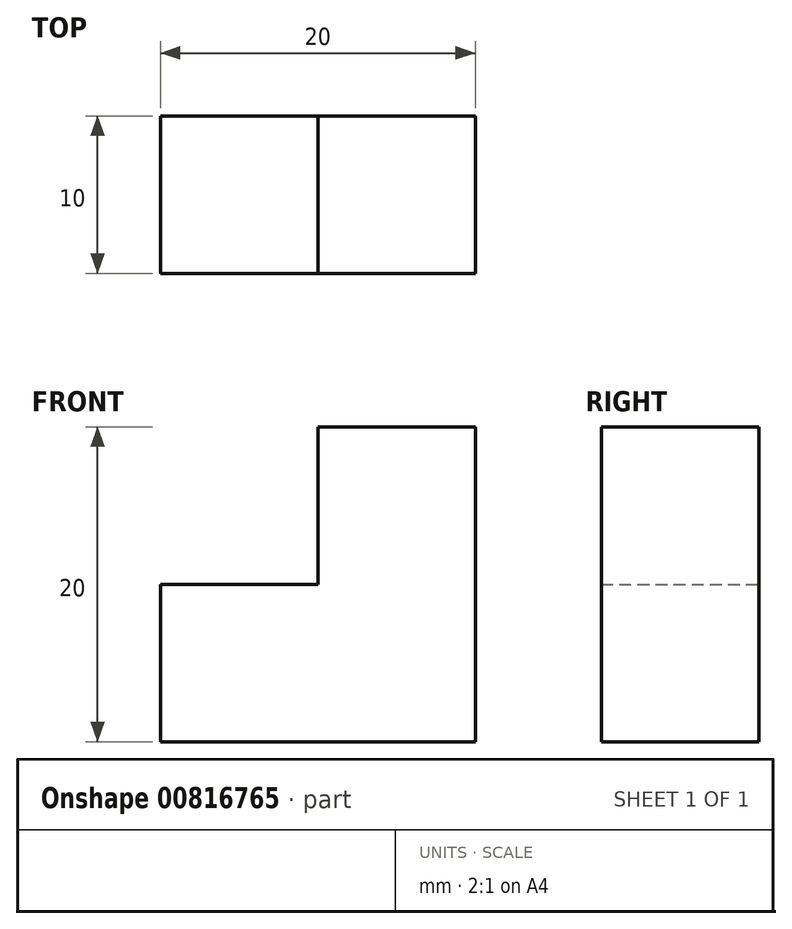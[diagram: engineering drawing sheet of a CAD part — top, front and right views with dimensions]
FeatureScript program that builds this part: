
annotation { "Feature Type Name" : "Feature", "Feature Type Description" : "" }
export const myFeature = defineFeature(function(context is Context, id is Id, definition is map)
    precondition{}
    {
        {
            var Q0;
            Q0=qCreatedBy(makeId("Top.planeOp"),FACE);
            var sketch = newSketch(context, id + "F0", { "sketchPlane" : qUnion([Q0])});
            skLineSegment(sketch, "E0.bottom", {"start": v(0, 0) * mm, "end": v(10, 0) * mm});
            skLineSegment(sketch, "E0.top", {"start": v(0, 10) * mm, "end": v(10, 10) * mm});
            skLineSegment(sketch, "E0.left", {"start": v(0, 0) * mm, "end": v(0, 10) * mm});
            skLineSegment(sketch, "E0.right", {"start": v(10, 0) * mm, "end": v(10, 10) * mm});
            skSolve(sketch);
        }
        {
            var Q0;
            Q0=makeQuery(id+"F0.imprint","IMPRINT",FACE,{"disambiguationData":[TD([[makeQuery(id+"F0.imprint","IMPRINT",EDGE,{"derivedFrom":sQuery(id+"F0.wireOp",EDGE,"E0.bottom")}),1.0]])]});
            extrude(context, id + "F1", {"entities" : qUnion([Q0]), "depth" : 10 * mm, "offsetDistance" : 25 * mm});
        }
        {
            var Q0;
            Q0=makeQuery(id+"F1.opExtrude","SWEPT_FACE",FACE,{"disambiguationData":[OSD([sQuery(id+"F0.wireOp",EDGE,"E0.left")])]});
            var sketch = newSketch(context, id + "F2", { "sketchPlane" : qUnion([Q0])});
            skLineSegment(sketch, "E1.bottom", {"start": v(0, 0) * mm, "end": v(-10, 0) * mm});
            skLineSegment(sketch, "E1.top", {"start": v(0, 10) * mm, "end": v(-10, 10) * mm});
            skLineSegment(sketch, "E1.left", {"start": v(0, 0) * mm, "end": v(0, 10) * mm});
            skLineSegment(sketch, "E1.right", {"start": v(-10, 0) * mm, "end": v(-10, 10) * mm});
            skSolve(sketch);
        }
        {
            var Q0;
            Q0=makeQuery(id+"F2.imprint","IMPRINT",FACE,{"disambiguationData":[TD([[makeQuery(id+"F2.imprint","IMPRINT",EDGE,{"derivedFrom":sQuery(id+"F2.wireOp",EDGE,"E1.bottom")}),-1.0]])]});
            extrude(context, id + "F3", {"entities" : qUnion([Q0]), "operationType" : NewBodyOperationType.ADD, "depth" : 10 * mm, "offsetDistance" : 25 * mm});
        }
        {
            var Q0;
            Q0=makeQuery(id+"F3.boolean.opBoolean","MERGE",FACE,{"derivedFrom":[makeQuery(id+"F1.opExtrude","CAP_FACE",FACE,{"disambiguationData":[OSD([sQuery(id+"F0.wireOp",EDGE,"E0.bottom"),sQuery(id+"F0.wireOp",EDGE,"E0.top"),sQuery(id+"F0.wireOp",EDGE,"E0.left"),sQuery(id+"F0.wireOp",EDGE,"E0.right")])],"isStart":false}),makeQuery(id+"F3.opExtrude","SWEPT_FACE",FACE,{"disambiguationData":[OSD([sQuery(id+"F2.wireOp",EDGE,"E1.top")])]})]});
            var sketch = newSketch(context, id + "F4", { "sketchPlane" : qUnion([Q0])});
            skLineSegment(sketch, "E2.bottom", {"start": v(0, 0) * mm, "end": v(10, 0) * mm});
            skLineSegment(sketch, "E2.top", {"start": v(0, 10) * mm, "end": v(10, 10) * mm});
            skLineSegment(sketch, "E2.left", {"start": v(0, 0) * mm, "end": v(0, 10) * mm});
            skLineSegment(sketch, "E2.right", {"start": v(10, 0) * mm, "end": v(10, 10) * mm});
            skSolve(sketch);
        }
        {
            var Q0;
            Q0=makeQuery(id+"F4.imprint","IMPRINT",FACE,{"disambiguationData":[TD([[makeQuery(id+"F4.imprint","IMPRINT",EDGE,{"derivedFrom":sQuery(id+"F4.wireOp",EDGE,"E2.bottom")}),1.0]])]});
            extrude(context, id + "F5", {"entities" : qUnion([Q0]), "operationType" : NewBodyOperationType.ADD, "depth" : 10 * mm, "offsetDistance" : 25 * mm});
        }
    });
